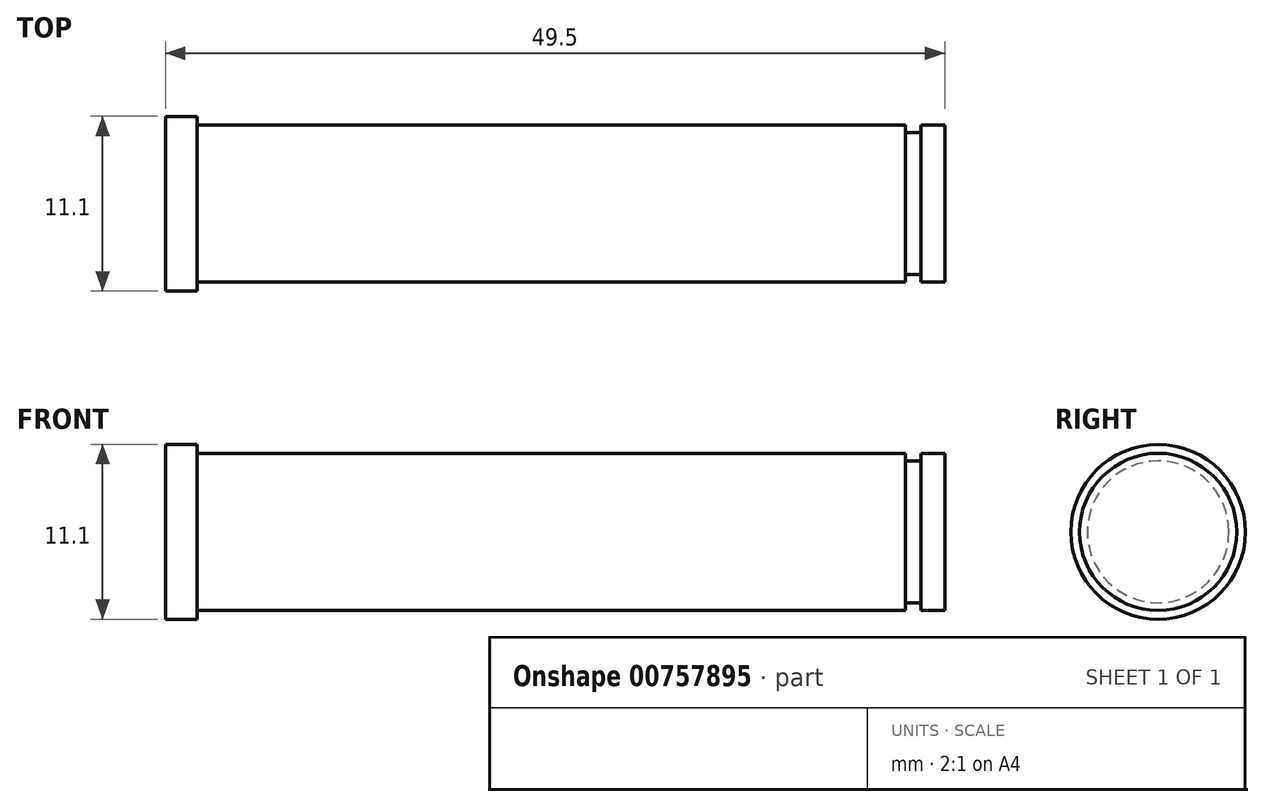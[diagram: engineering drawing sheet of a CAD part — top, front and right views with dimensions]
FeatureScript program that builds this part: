
annotation { "Feature Type Name" : "Feature", "Feature Type Description" : "" }
export const myFeature = defineFeature(function(context is Context, id is Id, definition is map)
    precondition{}
    {
        {
            var Q0;
            Q0=qCreatedBy(makeId("Right.planeOp"),FACE);
            var sketch = newSketch(context, id + "F0", { "sketchPlane" : qUnion([Q0])});
            skCircle(sketch, "E0", {"center": v(0, 0) * mm, "radius": 5 * mm});
            skSolve(sketch);
        }
        {
            var Q0;
            Q0=makeQuery(id+"F0.imprint","IMPRINT",FACE,{"disambiguationData":[TD([[makeQuery(id+"F0.imprint","IMPRINT",EDGE,{"derivedFrom":sQuery(id+"F0.wireOp",EDGE,"E0")}),1.0]])]});
            extrude(context, id + "F1", {"entities" : qUnion([Q0]), "depth" : 45 * mm, "offsetDistance" : 25 * mm});
        }
        {
            var Q0;
            Q0=makeQuery(id+"F1.opExtrude","CAP_FACE",FACE,{"disambiguationData":[OSD([sQuery(id+"F0.wireOp",EDGE,"E0")])],"isStart":true});
            var sketch = newSketch(context, id + "F2", { "sketchPlane" : qUnion([Q0])});
            skCircle(sketch, "E1", {"center": v(0, 0) * mm, "radius": 5.55 * mm});
            skSolve(sketch);
        }
        {
            var Q0;
            Q0=makeQuery(id+"F2.imprint","IMPRINT",FACE,{"disambiguationData":[TD([[makeQuery(id+"F2.imprint","IMPRINT",EDGE,{"derivedFrom":sQuery(id+"F2.wireOp",EDGE,"E1")}),1.0]])]});
            var Q1;
            Q1=makeQuery(id+"F2.imprint","IMPRINT",FACE,{"disambiguationData":[TD([[makeQuery(id+"F2.imprint","IMPRINT",EDGE,{"derivedFrom":makeQuery(id+"F1.opExtrude","CAP_EDGE",EDGE,{"disambiguationData":[OSD([sQuery(id+"F0.wireOp",EDGE,"E0")])],"isStart":true})}),-1.0]])]});
            extrude(context, id + "F3", {"entities" : qUnion([Q0, Q1]), "operationType" : NewBodyOperationType.ADD, "depth" : 2 * mm, "offsetDistance" : 25 * mm});
        }
        {
            var Q0;
            Q0=makeQuery(id+"F1.opExtrude","CAP_FACE",FACE,{"disambiguationData":[OSD([sQuery(id+"F0.wireOp",EDGE,"E0")])],"isStart":false});
            var sketch = newSketch(context, id + "F4", { "sketchPlane" : qUnion([Q0])});
            skCircle(sketch, "E2", {"center": v(0, 0) * mm, "radius": 4.5 * mm});
            skSolve(sketch);
        }
        {
            var Q0;
            Q0=makeQuery(id+"F4.imprint","IMPRINT",FACE,{"disambiguationData":[TD([[makeQuery(id+"F4.imprint","IMPRINT",EDGE,{"derivedFrom":sQuery(id+"F4.wireOp",EDGE,"E2")}),1.0]])]});
            extrude(context, id + "F5", {"entities" : qUnion([Q0]), "operationType" : NewBodyOperationType.ADD, "depth" : 1 * mm, "offsetDistance" : 25 * mm});
        }
        {
            var Q0;
            Q0=makeQuery(id+"F5.opExtrude","CAP_FACE",FACE,{"disambiguationData":[OSD([sQuery(id+"F4.wireOp",EDGE,"E2")])],"isStart":false});
            var sketch = newSketch(context, id + "F6", { "sketchPlane" : qUnion([Q0])});
            skCircle(sketch, "E3", {"center": v(0, 0) * mm, "radius": 5 * mm});
            skSolve(sketch);
        }
        {
            var Q0;
            Q0=makeQuery(id+"F6.imprint","IMPRINT",FACE,{"disambiguationData":[TD([[makeQuery(id+"F6.imprint","IMPRINT",EDGE,{"derivedFrom":sQuery(id+"F6.wireOp",EDGE,"E3")}),1.0]])]});
            var Q1;
            Q1=makeQuery(id+"F6.imprint","IMPRINT",FACE,{"disambiguationData":[TD([[makeQuery(id+"F6.imprint","IMPRINT",EDGE,{"derivedFrom":makeQuery(id+"F5.opExtrude","CAP_EDGE",EDGE,{"disambiguationData":[OSD([sQuery(id+"F4.wireOp",EDGE,"E2")])],"isStart":false})}),1.0]])]});
            extrude(context, id + "F7", {"entities" : qUnion([Q0, Q1]), "operationType" : NewBodyOperationType.ADD, "depth" : 1.5 * mm, "offsetDistance" : 25 * mm});
        }
    });
